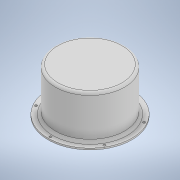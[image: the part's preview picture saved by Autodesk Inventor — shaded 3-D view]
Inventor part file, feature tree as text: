
AUTODESK INVENTOR PART (.ipt)
format: ipt  version: 2021 (Build 250183000, 183)  size: 187,904 bytes
history: native  units: mm
features: sketch x2, revolve x1, hole x1, fillet x1, projected_geometry x1
ambient origin geometry x8: Origin, YZ Plane, XZ Plane, XY Plane, X Axis, Y Axis, Z Axis, Center Point
bodies: Solid1 (feature_tree)
feature tree (6):
  revolve  "Revolution1"  [1 undecoded]
  hole  "Hole1"  [1 undecoded]
  fillet  "Fillet1"  [1 undecoded]
  sketch  "Sketch1"  dims[d3=90.0deg d5=81.5mm]
  sketch  "Sketch2"  dims[d7=9.0mm d8=5.0mm d9=45.0deg d10=16.0mm d11=3.0mm d16=4.5mm d17=8.0mm d18=60.0mm d20=360.0deg d22=4.5mm d23=10.0mm d24=9.4mm d25=2.0mm d26=90.0deg d27=13.0mm d28=20.594885mm d29=4.5mm d30=2.0mm d32=2.0mm d33=5.0mm d34=87.0mm]
  projected_geometry  "Projected Loop1"
note: 3 required parameter values undecoded (feature->parameter linkage not recoverable at this tier; creation-order binding heuristic only, values carry confidence <= 0.55)